# Revit family: SHWB105_Shenley semi-recessed 400 basin, RHTH Rev01
name_source: partatom
category: Generic Models
revit_build: Autodesk Revit 2015 (Build: 20140606_1530(x64)
units: mm (PartAtom-declared; Revit-internal decimal feet)

## types (1)
- SWC_WHB_SHWB105
    Basin mounting = Vanity mounted
    Brand = SanCeram
    Help = http://www.theswc.co.uk
    Manufacturer URL = www.theswc.co.uk
    NBS Reference Code = N13 - 335
    NBS Reference Description = WASH BASINS
    Name = Shenley semi-recessed 400 basin, RHTH
    Nominal Depth = 175 mm
    Nominal Length = 325 mm
    Nominal Width = 400 mm
    Overflow = Central Overflow
    Primary Finishes = Alpine White
    Primary Material = Vitreous China
    Product Family = Sanitary
    Product Group = recessed basins
    Product Information = http://www.theswc.co.uk
    Product SKU = SHWB105
    Spare Parts = http://www.theswc.co.uk
    Tap Holes = right hand tap hole
    Wash hand basin type = Semi-recessed basin
    Waste size = 1 1/4"
    Waste type = Slotted
    Weight = 8.1 kg

## geometry (parser evidence)
native form markers: Blend x6, Sweep x5
no freeform markers — native parametric forms only
